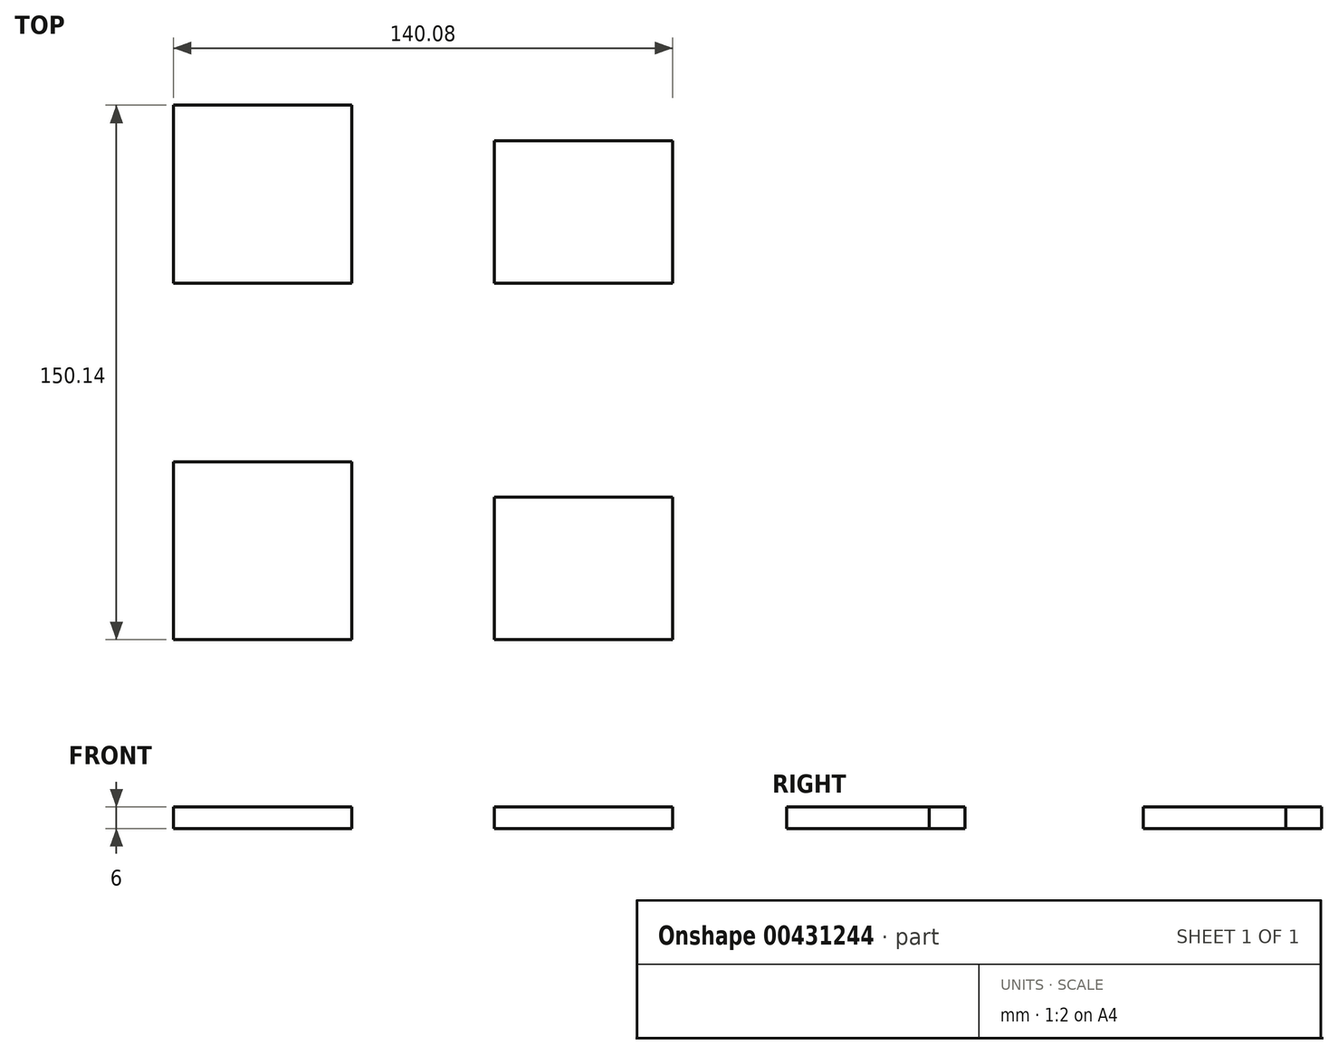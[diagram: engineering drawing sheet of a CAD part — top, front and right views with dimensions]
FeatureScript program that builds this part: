
annotation { "Feature Type Name" : "Feature", "Feature Type Description" : "" }
export const myFeature = defineFeature(function(context is Context, id is Id, definition is map)
    precondition{}
    {
        {
            var Q0;
            Q0=qCreatedBy(makeId("Top.planeOp"),FACE);
            var sketch = newSketch(context, id + "F0", { "sketchPlane" : qUnion([Q0])});
            skLineSegment(sketch, "E0.bottom", {"start": v(-90.2, 25.07) * mm, "end": v(-40.2, 25.07) * mm});
            skLineSegment(sketch, "E0.top", {"start": v(-90.2, 75.07) * mm, "end": v(-40.2, 75.07) * mm});
            skLineSegment(sketch, "E0.left", {"start": v(-90.2, 25.07) * mm, "end": v(-90.2, 75.07) * mm});
            skLineSegment(sketch, "E0.right", {"start": v(-40.2, 25.07) * mm, "end": v(-40.2, 75.07) * mm});
            skLineSegment(sketch, "E1.MirrorCS", {"start": v(-90.2, -75.07) * mm, "end": v(-40.2, -75.07) * mm});
            skLineSegment(sketch, "E2.MirrorCS", {"start": v(-40.2, -25.07) * mm, "end": v(-40.2, -75.07) * mm});
            skLineSegment(sketch, "E3.MirrorCS", {"start": v(-90.2, -25.07) * mm, "end": v(-90.2, -75.07) * mm});
            skLineSegment(sketch, "E4.MirrorCS", {"start": v(-90.2, -25.07) * mm, "end": v(-40.2, -25.07) * mm});
            skLineSegment(sketch, "E5.MirrorCS", {"start": v(49.88, 25.07) * mm, "end": v(-0.12, 25.07) * mm});
            skLineSegment(sketch, "E6.MirrorCS", {"start": v(49.88, -75.07) * mm, "end": v(-0.12, -75.07) * mm});
            skLineSegment(sketch, "E7.MirrorCS", {"start": v(49.88, 25.07) * mm, "end": v(49.88, 65.07) * mm});
            skLineSegment(sketch, "E8.MirrorCS", {"start": v(49.88, -35.07) * mm, "end": v(49.88, -75.07) * mm});
            skLineSegment(sketch, "E9.MirrorCS", {"start": v(-0.12, -35.07) * mm, "end": v(-0.12, -75.07) * mm});
            skLineSegment(sketch, "E10.MirrorCS", {"start": v(49.88, -35.07) * mm, "end": v(-0.12, -35.07) * mm});
            skLineSegment(sketch, "E11.MirrorCS", {"start": v(49.88, 65.07) * mm, "end": v(-0.12, 65.07) * mm});
            skLineSegment(sketch, "E12.MirrorCS", {"start": v(-0.12, 25.07) * mm, "end": v(-0.12, 65.07) * mm});
            skSolve(sketch);
        }
        {
            var Q0;
            Q0 = qSketchRegion(id + "F0", true);
            extrude(context, id + "F1", {"entities" : qUnion([Q0]), "depth" : 6 * mm});
        }
    });
